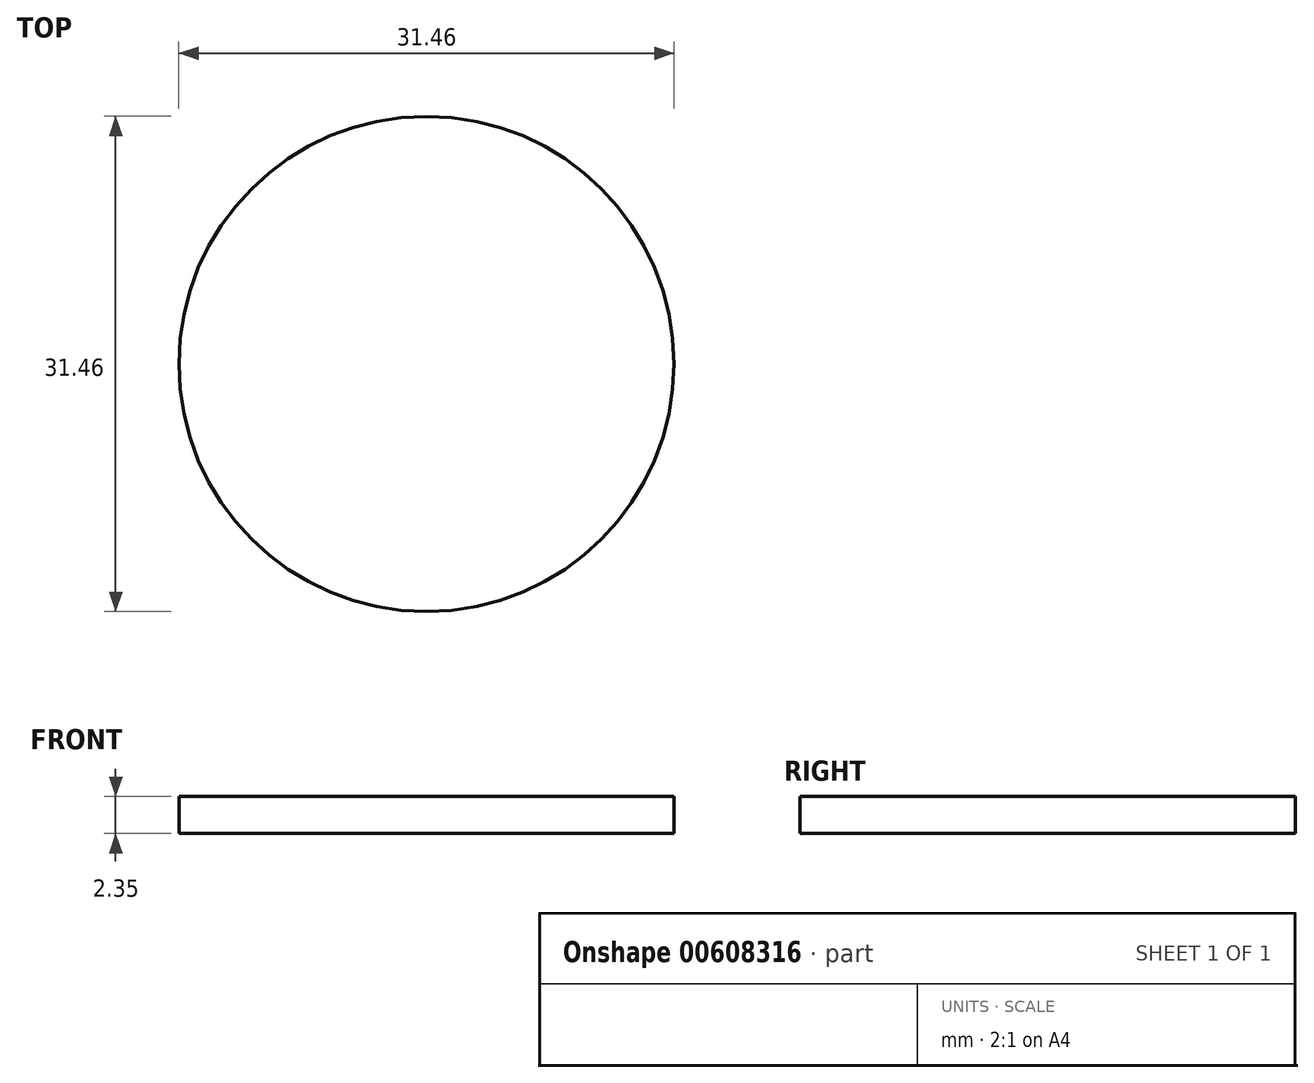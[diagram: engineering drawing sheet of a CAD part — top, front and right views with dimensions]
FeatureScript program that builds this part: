
annotation { "Feature Type Name" : "Feature", "Feature Type Description" : "" }
export const myFeature = defineFeature(function(context is Context, id is Id, definition is map)
    precondition{}
    {
        {
            var Q0;
            Q0=qCreatedBy(makeId("Top.planeOp"),FACE);
            var sketch = newSketch(context, id + "F0", { "sketchPlane" : qUnion([Q0])});
            skCircle(sketch, "E0", {"center": v(0, 0) * mm, "radius": 15.72 * mm});
            skSolve(sketch);
        }
        {
            var Q0;
            Q0=makeQuery(id+"F0.imprint","IMPRINT",FACE,{"disambiguationData":[TD([[makeQuery(id+"F0.imprint","IMPRINT",EDGE,{"derivedFrom":sQuery(id+"F0.wireOp",EDGE,"E0")}),1.0]])]});
            extrude(context, id + "F1", {"entities" : qUnion([Q0]), "depth" : 2.35 * mm, "offsetDistance" : 25 * mm});
        }
    });
